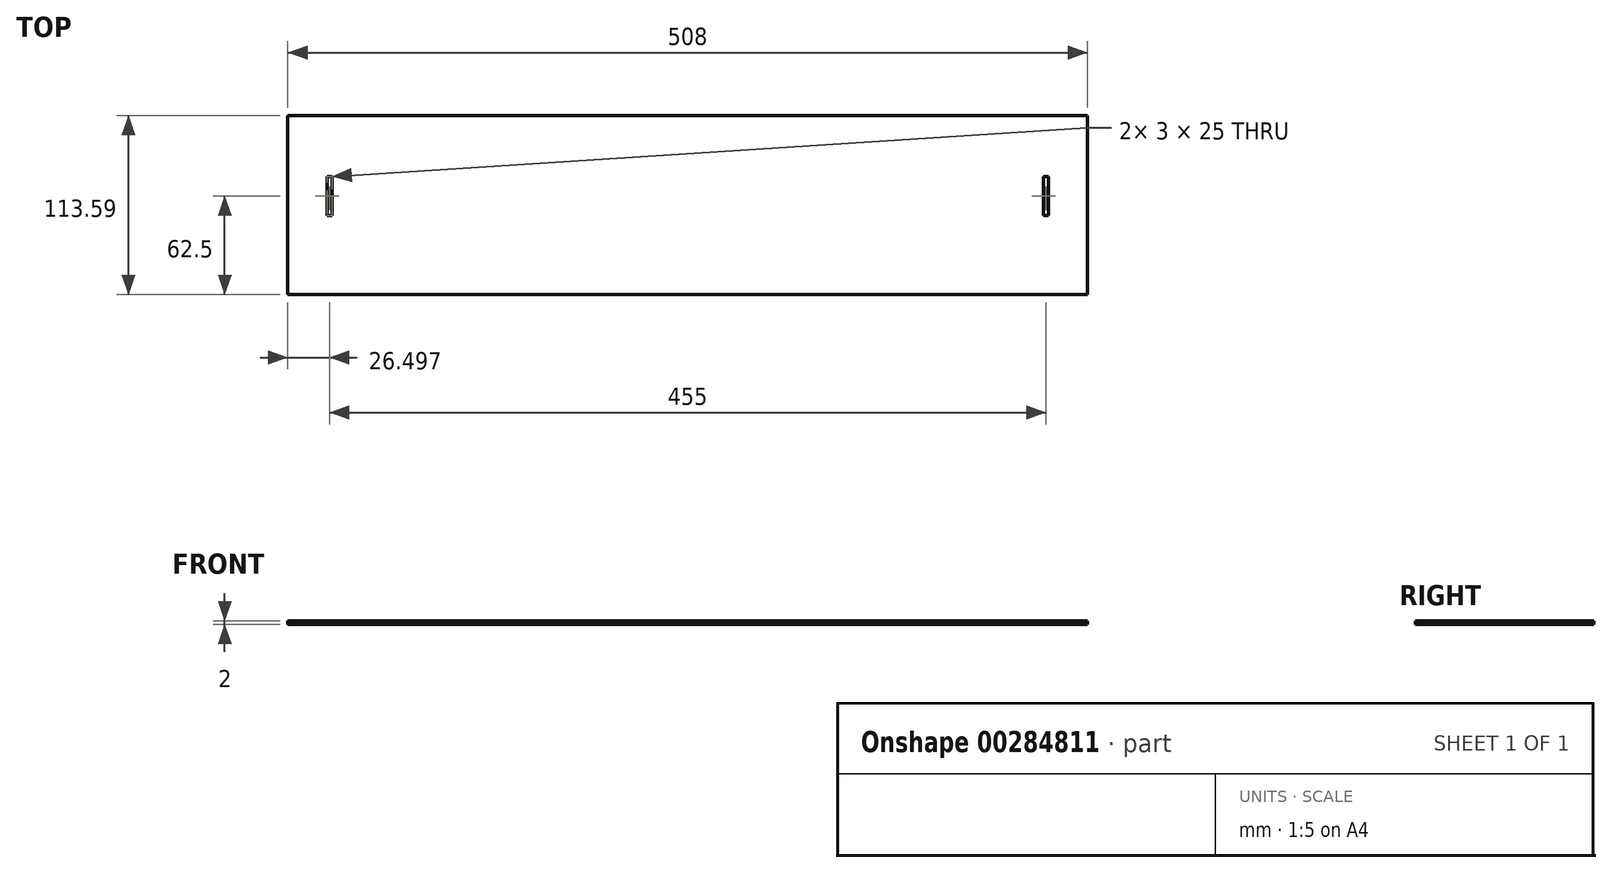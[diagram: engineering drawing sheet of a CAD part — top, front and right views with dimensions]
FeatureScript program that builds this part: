
annotation { "Feature Type Name" : "Feature", "Feature Type Description" : "" }
export const myFeature = defineFeature(function(context is Context, id is Id, definition is map)
    precondition{}
    {
        {
            var Q0;
            Q0=qCreatedBy(makeId("Top.planeOp"),FACE);
            var sketch = newSketch(context, id + "F0", { "sketchPlane" : qUnion([Q0])});
            skLineSegment(sketch, "E0.bottom", {"start": v(-272.36, 25.63) * mm, "end": v(235.64, 25.63) * mm});
            skLineSegment(sketch, "E0.top", {"start": v(-272.36, -87.96) * mm, "end": v(235.64, -87.96) * mm});
            skLineSegment(sketch, "E0.left", {"start": v(-272.36, 25.63) * mm, "end": v(-272.36, -87.96) * mm});
            skLineSegment(sketch, "E0.right", {"start": v(235.64, 25.63) * mm, "end": v(235.64, -87.96) * mm});
            skLineSegment(sketch, "E1.bottom", {"start": v(-247.36, -12.96) * mm, "end": v(-244.36, -12.96) * mm});
            skLineSegment(sketch, "E1.top", {"start": v(-247.36, -37.96) * mm, "end": v(-244.36, -37.96) * mm});
            skLineSegment(sketch, "E1.left", {"start": v(-247.36, -12.96) * mm, "end": v(-247.36, -37.96) * mm});
            skLineSegment(sketch, "E1.right", {"start": v(-244.36, -12.96) * mm, "end": v(-244.36, -37.96) * mm});
            skLineSegment(sketch, "E2.bottom", {"start": v(207.64, -12.96) * mm, "end": v(210.64, -12.96) * mm});
            skLineSegment(sketch, "E2.top", {"start": v(207.64, -37.96) * mm, "end": v(210.64, -37.96) * mm});
            skLineSegment(sketch, "E2.left", {"start": v(207.64, -12.96) * mm, "end": v(207.64, -37.96) * mm});
            skLineSegment(sketch, "E2.right", {"start": v(210.64, -12.96) * mm, "end": v(210.64, -37.96) * mm});
            skSolve(sketch);
        }
        {
            var Q0;
            Q0=makeQuery(id+"F0.imprint","IMPRINT",FACE,{"disambiguationData":[TD([[makeQuery(id+"F0.imprint","IMPRINT",EDGE,{"derivedFrom":sQuery(id+"F0.wireOp",EDGE,"E0.bottom")}),-1.0]])]});
            extrude(context, id + "F1", {"entities" : qUnion([Q0]), "depth" : 2 * mm, "offsetDistance" : 25 * mm});
        }
    });
